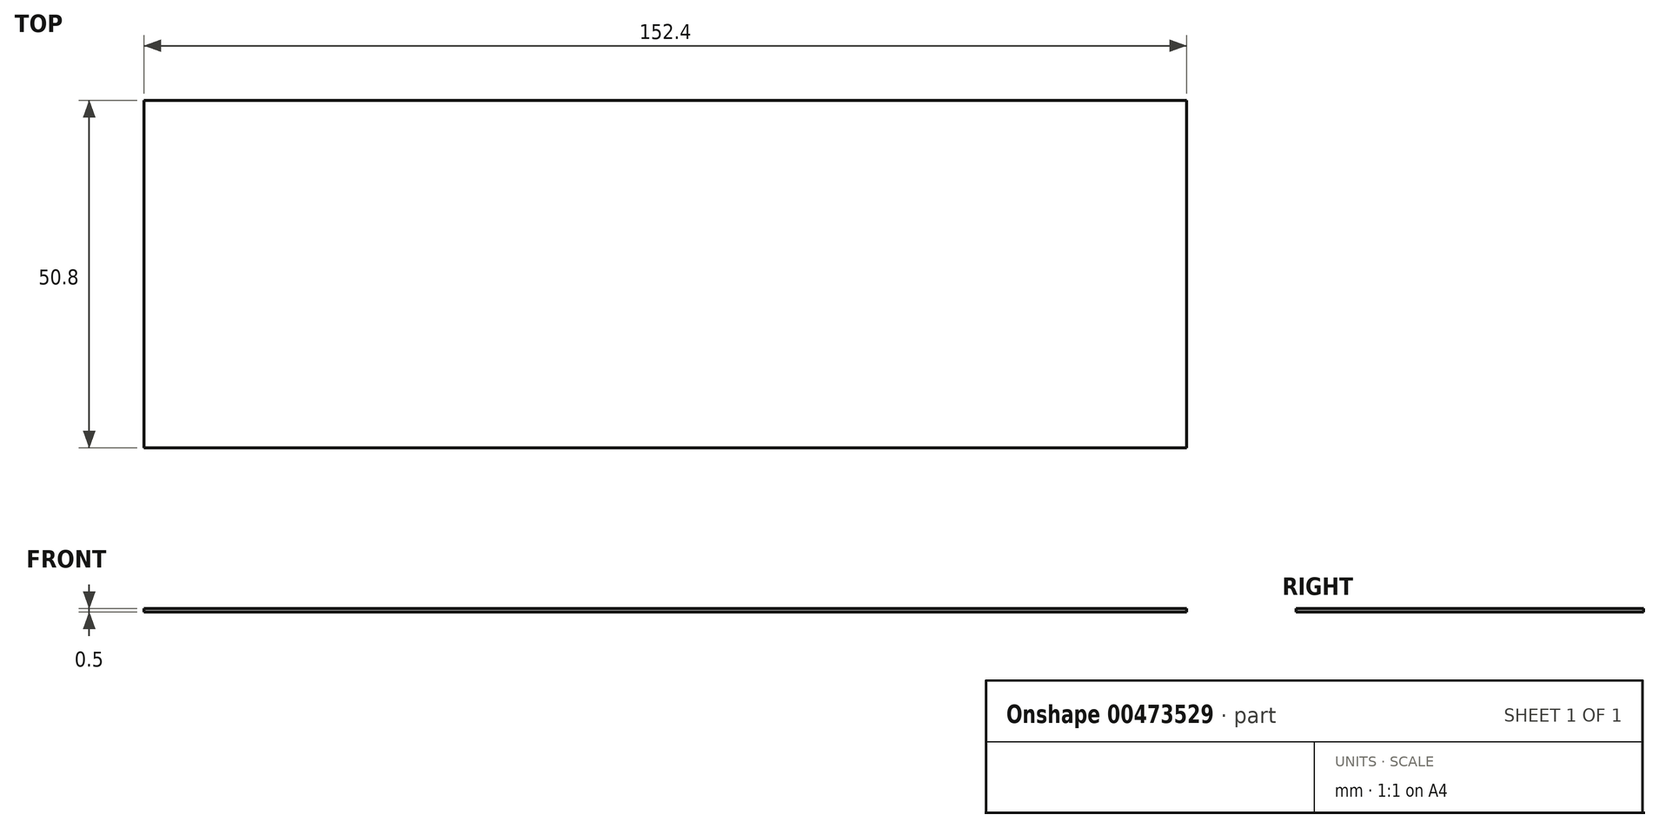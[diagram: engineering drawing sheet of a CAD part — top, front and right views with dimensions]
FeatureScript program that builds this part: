
annotation { "Feature Type Name" : "Feature", "Feature Type Description" : "" }
export const myFeature = defineFeature(function(context is Context, id is Id, definition is map)
    precondition{}
    {
        {
            var Q0;
            Q0=qCreatedBy(makeId("Top.planeOp"),FACE);
            var sketch = newSketch(context, id + "F0", { "sketchPlane" : qUnion([Q0])});
            skLineSegment(sketch, "E0.bottom", {"start": v(-76.2, 25.4) * mm, "end": v(76.2, 25.4) * mm});
            skLineSegment(sketch, "E0.top", {"start": v(-76.2, -25.4) * mm, "end": v(76.2, -25.4) * mm});
            skLineSegment(sketch, "E0.left", {"start": v(-76.2, 25.4) * mm, "end": v(-76.2, -25.4) * mm});
            skLineSegment(sketch, "E0.right", {"start": v(76.2, 25.4) * mm, "end": v(76.2, -25.4) * mm});
            skLineSegment(sketch, "E1", {"start": v(-76.2, -25.4) * mm, "end": v(76.2, 25.4) * mm, "construction": true});
            skSolve(sketch);
        }
        {
            var Q0;
            Q0 = qSketchRegion(id + "F0", true);
            extrude(context, id + "F1", {"entities" : qUnion([Q0]), "endBound" : BoundingType.SYMMETRIC, "depth" : 0.5 * mm});
        }
    });
